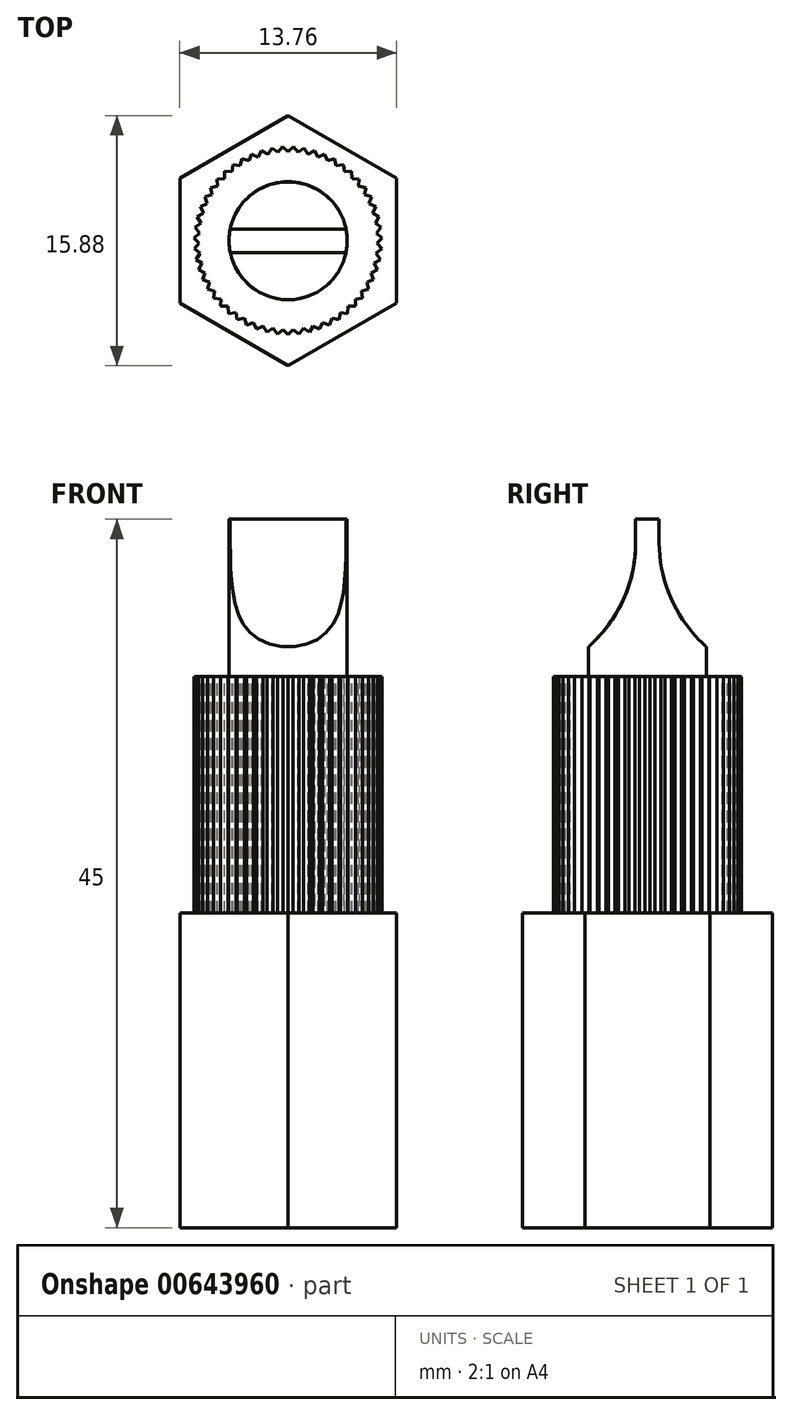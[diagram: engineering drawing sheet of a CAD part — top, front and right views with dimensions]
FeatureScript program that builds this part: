
annotation { "Feature Type Name" : "Feature", "Feature Type Description" : "" }
export const myFeature = defineFeature(function(context is Context, id is Id, definition is map)
    precondition{}
    {
        {
            var Q0;
            Q0=qCreatedBy(makeId("Top.planeOp"),FACE);
            var sketch = newSketch(context, id + "F0", { "sketchPlane" : qUnion([Q0])});
            skCircle(sketch, "E0.cCircle", {"center": v(0, 0) * mm, "radius": 7.94 * mm, "construction": true});
            skLineSegment(sketch, "E0.0", {"start": v(6.87, 3.97) * mm, "end": v(6.88, -3.97) * mm});
            skLineSegment(sketch, "E0.1", {"start": v(6.88, -3.97) * mm, "end": v(0, -7.94) * mm});
            skLineSegment(sketch, "E0.2", {"start": v(0, -7.94) * mm, "end": v(-6.88, -3.97) * mm});
            skLineSegment(sketch, "E0.3", {"start": v(-6.87, -3.97) * mm, "end": v(-6.88, 3.97) * mm});
            skLineSegment(sketch, "E0.4", {"start": v(-6.88, 3.97) * mm, "end": v(0, 7.94) * mm});
            skLineSegment(sketch, "E0.5", {"start": v(0, 7.94) * mm, "end": v(6.87, 3.97) * mm});
            skSolve(sketch);
        }
        {
            var Q0;
            Q0 = qSketchRegion(id + "F0", true);
            extrude(context, id + "F1", {"entities" : qUnion([Q0]), "depth" : 20 * mm, "offsetDistance" : 25 * mm});
        }
        {
            var Q0;
            Q0=makeQuery(id+"F1.opExtrude","CAP_FACE",FACE,{"disambiguationData":[OSD([sQuery(id+"F0.wireOp",EDGE,"E0.0"),sQuery(id+"F0.wireOp",EDGE,"E0.1"),sQuery(id+"F0.wireOp",EDGE,"E0.2"),sQuery(id+"F0.wireOp",EDGE,"E0.3"),sQuery(id+"F0.wireOp",EDGE,"E0.4"),sQuery(id+"F0.wireOp",EDGE,"E0.5")])],"isStart":false});
            var sketch = newSketch(context, id + "F2", { "sketchPlane" : qUnion([Q0])});
            skCircle(sketch, "E1", {"center": v(0, 0) * mm, "radius": 6 * mm});
            skSolve(sketch);
        }
        {
            var Q0;
            Q0=makeQuery(id+"F2.imprint","IMPRINT",FACE,{"disambiguationData":[TD([[makeQuery(id+"F2.imprint","IMPRINT",EDGE,{"derivedFrom":sQuery(id+"F2.wireOp",EDGE,"E1")}),1.0]])]});
            extrude(context, id + "F3", {"entities" : qUnion([Q0]), "operationType" : NewBodyOperationType.ADD, "depth" : 15 * mm, "offsetDistance" : 25 * mm});
        }
        {
            var Q0;
            Q0=makeQuery(id+"F3.opExtrude","CAP_FACE",FACE,{"disambiguationData":[OSD([sQuery(id+"F2.wireOp",EDGE,"E1")])],"isStart":false});
            var sketch = newSketch(context, id + "F4", { "sketchPlane" : qUnion([Q0])});
            skLineSegment(sketch, "E2", {"start": v(0, 0) * mm, "end": v(0, 6) * mm, "construction": true});
            skLineSegment(sketch, "E3", {"start": v(-0.37, 5.99) * mm, "end": v(0, 5.65) * mm});
            skLineSegment(sketch, "E4", {"start": v(0.37, 5.99) * mm, "end": v(0, 5.65) * mm});
            skSolve(sketch);
        }
        {
            var Q0;
            {var subQ0=sQuery(id+"F4.wireOp",EDGE,"E3");Q0=makeQuery(id+"F4.imprint","IMPRINT",FACE,{"disambiguationData":[TD([[makeQuery(id+"F4.imprint","IMPRINT",EDGE,{"derivedFrom":subQ0}),1.0]])]});}
            var Q1;
            Q1=makeQuery(id+"F1.opExtrude","CAP_FACE",FACE,{"disambiguationData":[OSD([sQuery(id+"F0.wireOp",EDGE,"E0.0"),sQuery(id+"F0.wireOp",EDGE,"E0.1"),sQuery(id+"F0.wireOp",EDGE,"E0.2"),sQuery(id+"F0.wireOp",EDGE,"E0.3"),sQuery(id+"F0.wireOp",EDGE,"E0.4"),sQuery(id+"F0.wireOp",EDGE,"E0.5")])],"isStart":false});
            extrude(context, id + "F5", {"entities" : qUnion([Q0]), "endBound" : BoundingType.UP_TO_SURFACE, "oppositeDirection" : true, "depth" : 25 * mm, "endBoundEntityFace" : qUnion([Q1]), "offsetDistance" : 25 * mm});
        }
        {
            var Q0;
            Q0=makeQuery(id+"F5.opExtrude","SWEPT_BODY",BODY,{"disambiguationData":[OSD([sQuery(id+"F2.wireOp",EDGE,"E1"),sQuery(id+"F4.wireOp",EDGE,"E3"),sQuery(id+"F4.wireOp",EDGE,"E4")])]});
            var Q1;
            Q1=makeQuery(id+"F3.opExtrude","CAP_EDGE",EDGE,{"disambiguationData":[OSD([sQuery(id+"F2.wireOp",EDGE,"E1")])],"isStart":false});
            circularPattern(context, id + "F6", {"entities" : qUnion([Q0]), "axis" : qUnion([Q1]), "angle" : 360 * degree, "instanceCount" : 55, "oppositeDirection" : true, "equalSpace" : true});
        }
        {
            var Q0;
            Q0=makeQuery(id+"F6.opPattern","COPY",BODY,{"derivedFrom":makeQuery(id+"F5.opExtrude","SWEPT_BODY",BODY,{"disambiguationData":[OSD([sQuery(id+"F2.wireOp",EDGE,"E1"),sQuery(id+"F4.wireOp",EDGE,"E3"),sQuery(id+"F4.wireOp",EDGE,"E4")])]}),"instanceName":"6"});
            var Q1;
            Q1=makeQuery(id+"F6.opPattern","COPY",BODY,{"derivedFrom":makeQuery(id+"F5.opExtrude","SWEPT_BODY",BODY,{"disambiguationData":[OSD([sQuery(id+"F2.wireOp",EDGE,"E1"),sQuery(id+"F4.wireOp",EDGE,"E3"),sQuery(id+"F4.wireOp",EDGE,"E4")])]}),"instanceName":"8"});
            var Q2;
            Q2=makeQuery(id+"F6.opPattern","COPY",BODY,{"derivedFrom":makeQuery(id+"F5.opExtrude","SWEPT_BODY",BODY,{"disambiguationData":[OSD([sQuery(id+"F2.wireOp",EDGE,"E1"),sQuery(id+"F4.wireOp",EDGE,"E3"),sQuery(id+"F4.wireOp",EDGE,"E4")])]}),"instanceName":"10"});
            var Q3;
            Q3=makeQuery(id+"F6.opPattern","COPY",BODY,{"derivedFrom":makeQuery(id+"F5.opExtrude","SWEPT_BODY",BODY,{"disambiguationData":[OSD([sQuery(id+"F2.wireOp",EDGE,"E1"),sQuery(id+"F4.wireOp",EDGE,"E3"),sQuery(id+"F4.wireOp",EDGE,"E4")])]}),"instanceName":"7"});
            var Q4;
            Q4=makeQuery(id+"F6.opPattern","COPY",BODY,{"derivedFrom":makeQuery(id+"F5.opExtrude","SWEPT_BODY",BODY,{"disambiguationData":[OSD([sQuery(id+"F2.wireOp",EDGE,"E1"),sQuery(id+"F4.wireOp",EDGE,"E3"),sQuery(id+"F4.wireOp",EDGE,"E4")])]}),"instanceName":"1"});
            var Q5;
            Q5=makeQuery(id+"F6.opPattern","COPY",BODY,{"derivedFrom":makeQuery(id+"F5.opExtrude","SWEPT_BODY",BODY,{"disambiguationData":[OSD([sQuery(id+"F2.wireOp",EDGE,"E1"),sQuery(id+"F4.wireOp",EDGE,"E3"),sQuery(id+"F4.wireOp",EDGE,"E4")])]}),"instanceName":"4"});
            var Q6;
            Q6=makeQuery(id+"F6.opPattern","COPY",BODY,{"derivedFrom":makeQuery(id+"F5.opExtrude","SWEPT_BODY",BODY,{"disambiguationData":[OSD([sQuery(id+"F2.wireOp",EDGE,"E1"),sQuery(id+"F4.wireOp",EDGE,"E3"),sQuery(id+"F4.wireOp",EDGE,"E4")])]}),"instanceName":"5"});
            var Q7;
            Q7=makeQuery(id+"F6.opPattern","COPY",BODY,{"derivedFrom":makeQuery(id+"F5.opExtrude","SWEPT_BODY",BODY,{"disambiguationData":[OSD([sQuery(id+"F2.wireOp",EDGE,"E1"),sQuery(id+"F4.wireOp",EDGE,"E3"),sQuery(id+"F4.wireOp",EDGE,"E4")])]}),"instanceName":"3"});
            var Q8;
            Q8=makeQuery(id+"F6.opPattern","COPY",BODY,{"derivedFrom":makeQuery(id+"F5.opExtrude","SWEPT_BODY",BODY,{"disambiguationData":[OSD([sQuery(id+"F2.wireOp",EDGE,"E1"),sQuery(id+"F4.wireOp",EDGE,"E3"),sQuery(id+"F4.wireOp",EDGE,"E4")])]}),"instanceName":"2"});
            var Q9;
            Q9=makeQuery(id+"F5.opExtrude","SWEPT_BODY",BODY,{"disambiguationData":[OSD([sQuery(id+"F2.wireOp",EDGE,"E1"),sQuery(id+"F4.wireOp",EDGE,"E3"),sQuery(id+"F4.wireOp",EDGE,"E4")])]});
            var Q10;
            Q10=makeQuery(id+"F6.opPattern","COPY",BODY,{"derivedFrom":makeQuery(id+"F5.opExtrude","SWEPT_BODY",BODY,{"disambiguationData":[OSD([sQuery(id+"F2.wireOp",EDGE,"E1"),sQuery(id+"F4.wireOp",EDGE,"E3"),sQuery(id+"F4.wireOp",EDGE,"E4")])]}),"instanceName":"9"});
            var Q11;
            Q11=makeQuery(id+"F6.opPattern","COPY",BODY,{"derivedFrom":makeQuery(id+"F5.opExtrude","SWEPT_BODY",BODY,{"disambiguationData":[OSD([sQuery(id+"F2.wireOp",EDGE,"E1"),sQuery(id+"F4.wireOp",EDGE,"E3"),sQuery(id+"F4.wireOp",EDGE,"E4")])]}),"instanceName":"11"});
            var Q12;
            Q12=makeQuery(id+"F6.opPattern","COPY",BODY,{"derivedFrom":makeQuery(id+"F5.opExtrude","SWEPT_BODY",BODY,{"disambiguationData":[OSD([sQuery(id+"F2.wireOp",EDGE,"E1"),sQuery(id+"F4.wireOp",EDGE,"E3"),sQuery(id+"F4.wireOp",EDGE,"E4")])]}),"instanceName":"12"});
            var Q13;
            Q13=makeQuery(id+"F6.opPattern","COPY",BODY,{"derivedFrom":makeQuery(id+"F5.opExtrude","SWEPT_BODY",BODY,{"disambiguationData":[OSD([sQuery(id+"F2.wireOp",EDGE,"E1"),sQuery(id+"F4.wireOp",EDGE,"E3"),sQuery(id+"F4.wireOp",EDGE,"E4")])]}),"instanceName":"13"});
            var Q14;
            Q14=makeQuery(id+"F6.opPattern","COPY",BODY,{"derivedFrom":makeQuery(id+"F5.opExtrude","SWEPT_BODY",BODY,{"disambiguationData":[OSD([sQuery(id+"F2.wireOp",EDGE,"E1"),sQuery(id+"F4.wireOp",EDGE,"E3"),sQuery(id+"F4.wireOp",EDGE,"E4")])]}),"instanceName":"14"});
            var Q15;
            Q15=makeQuery(id+"F6.opPattern","COPY",BODY,{"derivedFrom":makeQuery(id+"F5.opExtrude","SWEPT_BODY",BODY,{"disambiguationData":[OSD([sQuery(id+"F2.wireOp",EDGE,"E1"),sQuery(id+"F4.wireOp",EDGE,"E3"),sQuery(id+"F4.wireOp",EDGE,"E4")])]}),"instanceName":"15"});
            var Q16;
            Q16=makeQuery(id+"F6.opPattern","COPY",BODY,{"derivedFrom":makeQuery(id+"F5.opExtrude","SWEPT_BODY",BODY,{"disambiguationData":[OSD([sQuery(id+"F2.wireOp",EDGE,"E1"),sQuery(id+"F4.wireOp",EDGE,"E3"),sQuery(id+"F4.wireOp",EDGE,"E4")])]}),"instanceName":"16"});
            var Q17;
            Q17=makeQuery(id+"F6.opPattern","COPY",BODY,{"derivedFrom":makeQuery(id+"F5.opExtrude","SWEPT_BODY",BODY,{"disambiguationData":[OSD([sQuery(id+"F2.wireOp",EDGE,"E1"),sQuery(id+"F4.wireOp",EDGE,"E3"),sQuery(id+"F4.wireOp",EDGE,"E4")])]}),"instanceName":"17"});
            var Q18;
            Q18=makeQuery(id+"F6.opPattern","COPY",BODY,{"derivedFrom":makeQuery(id+"F5.opExtrude","SWEPT_BODY",BODY,{"disambiguationData":[OSD([sQuery(id+"F2.wireOp",EDGE,"E1"),sQuery(id+"F4.wireOp",EDGE,"E3"),sQuery(id+"F4.wireOp",EDGE,"E4")])]}),"instanceName":"18"});
            var Q19;
            Q19=makeQuery(id+"F6.opPattern","COPY",BODY,{"derivedFrom":makeQuery(id+"F5.opExtrude","SWEPT_BODY",BODY,{"disambiguationData":[OSD([sQuery(id+"F2.wireOp",EDGE,"E1"),sQuery(id+"F4.wireOp",EDGE,"E3"),sQuery(id+"F4.wireOp",EDGE,"E4")])]}),"instanceName":"19"});
            var Q20;
            Q20=makeQuery(id+"F6.opPattern","COPY",BODY,{"derivedFrom":makeQuery(id+"F5.opExtrude","SWEPT_BODY",BODY,{"disambiguationData":[OSD([sQuery(id+"F2.wireOp",EDGE,"E1"),sQuery(id+"F4.wireOp",EDGE,"E3"),sQuery(id+"F4.wireOp",EDGE,"E4")])]}),"instanceName":"20"});
            var Q21;
            Q21=makeQuery(id+"F6.opPattern","COPY",BODY,{"derivedFrom":makeQuery(id+"F5.opExtrude","SWEPT_BODY",BODY,{"disambiguationData":[OSD([sQuery(id+"F2.wireOp",EDGE,"E1"),sQuery(id+"F4.wireOp",EDGE,"E3"),sQuery(id+"F4.wireOp",EDGE,"E4")])]}),"instanceName":"21"});
            var Q22;
            Q22=makeQuery(id+"F6.opPattern","COPY",BODY,{"derivedFrom":makeQuery(id+"F5.opExtrude","SWEPT_BODY",BODY,{"disambiguationData":[OSD([sQuery(id+"F2.wireOp",EDGE,"E1"),sQuery(id+"F4.wireOp",EDGE,"E3"),sQuery(id+"F4.wireOp",EDGE,"E4")])]}),"instanceName":"22"});
            var Q23;
            Q23=makeQuery(id+"F6.opPattern","COPY",BODY,{"derivedFrom":makeQuery(id+"F5.opExtrude","SWEPT_BODY",BODY,{"disambiguationData":[OSD([sQuery(id+"F2.wireOp",EDGE,"E1"),sQuery(id+"F4.wireOp",EDGE,"E3"),sQuery(id+"F4.wireOp",EDGE,"E4")])]}),"instanceName":"23"});
            var Q24;
            Q24=makeQuery(id+"F6.opPattern","COPY",BODY,{"derivedFrom":makeQuery(id+"F5.opExtrude","SWEPT_BODY",BODY,{"disambiguationData":[OSD([sQuery(id+"F2.wireOp",EDGE,"E1"),sQuery(id+"F4.wireOp",EDGE,"E3"),sQuery(id+"F4.wireOp",EDGE,"E4")])]}),"instanceName":"24"});
            var Q25;
            Q25=makeQuery(id+"F6.opPattern","COPY",BODY,{"derivedFrom":makeQuery(id+"F5.opExtrude","SWEPT_BODY",BODY,{"disambiguationData":[OSD([sQuery(id+"F2.wireOp",EDGE,"E1"),sQuery(id+"F4.wireOp",EDGE,"E3"),sQuery(id+"F4.wireOp",EDGE,"E4")])]}),"instanceName":"25"});
            var Q26;
            Q26=makeQuery(id+"F6.opPattern","COPY",BODY,{"derivedFrom":makeQuery(id+"F5.opExtrude","SWEPT_BODY",BODY,{"disambiguationData":[OSD([sQuery(id+"F2.wireOp",EDGE,"E1"),sQuery(id+"F4.wireOp",EDGE,"E3"),sQuery(id+"F4.wireOp",EDGE,"E4")])]}),"instanceName":"26"});
            var Q27;
            Q27=makeQuery(id+"F6.opPattern","COPY",BODY,{"derivedFrom":makeQuery(id+"F5.opExtrude","SWEPT_BODY",BODY,{"disambiguationData":[OSD([sQuery(id+"F2.wireOp",EDGE,"E1"),sQuery(id+"F4.wireOp",EDGE,"E3"),sQuery(id+"F4.wireOp",EDGE,"E4")])]}),"instanceName":"27"});
            var Q28;
            Q28=makeQuery(id+"F6.opPattern","COPY",BODY,{"derivedFrom":makeQuery(id+"F5.opExtrude","SWEPT_BODY",BODY,{"disambiguationData":[OSD([sQuery(id+"F2.wireOp",EDGE,"E1"),sQuery(id+"F4.wireOp",EDGE,"E3"),sQuery(id+"F4.wireOp",EDGE,"E4")])]}),"instanceName":"28"});
            var Q29;
            Q29=makeQuery(id+"F6.opPattern","COPY",BODY,{"derivedFrom":makeQuery(id+"F5.opExtrude","SWEPT_BODY",BODY,{"disambiguationData":[OSD([sQuery(id+"F2.wireOp",EDGE,"E1"),sQuery(id+"F4.wireOp",EDGE,"E3"),sQuery(id+"F4.wireOp",EDGE,"E4")])]}),"instanceName":"29"});
            var Q30;
            Q30=makeQuery(id+"F6.opPattern","COPY",BODY,{"derivedFrom":makeQuery(id+"F5.opExtrude","SWEPT_BODY",BODY,{"disambiguationData":[OSD([sQuery(id+"F2.wireOp",EDGE,"E1"),sQuery(id+"F4.wireOp",EDGE,"E3"),sQuery(id+"F4.wireOp",EDGE,"E4")])]}),"instanceName":"30"});
            var Q31;
            Q31=makeQuery(id+"F6.opPattern","COPY",BODY,{"derivedFrom":makeQuery(id+"F5.opExtrude","SWEPT_BODY",BODY,{"disambiguationData":[OSD([sQuery(id+"F2.wireOp",EDGE,"E1"),sQuery(id+"F4.wireOp",EDGE,"E3"),sQuery(id+"F4.wireOp",EDGE,"E4")])]}),"instanceName":"31"});
            var Q32;
            Q32=makeQuery(id+"F6.opPattern","COPY",BODY,{"derivedFrom":makeQuery(id+"F5.opExtrude","SWEPT_BODY",BODY,{"disambiguationData":[OSD([sQuery(id+"F2.wireOp",EDGE,"E1"),sQuery(id+"F4.wireOp",EDGE,"E3"),sQuery(id+"F4.wireOp",EDGE,"E4")])]}),"instanceName":"32"});
            var Q33;
            Q33=makeQuery(id+"F6.opPattern","COPY",BODY,{"derivedFrom":makeQuery(id+"F5.opExtrude","SWEPT_BODY",BODY,{"disambiguationData":[OSD([sQuery(id+"F2.wireOp",EDGE,"E1"),sQuery(id+"F4.wireOp",EDGE,"E3"),sQuery(id+"F4.wireOp",EDGE,"E4")])]}),"instanceName":"33"});
            var Q34;
            Q34=makeQuery(id+"F6.opPattern","COPY",BODY,{"derivedFrom":makeQuery(id+"F5.opExtrude","SWEPT_BODY",BODY,{"disambiguationData":[OSD([sQuery(id+"F2.wireOp",EDGE,"E1"),sQuery(id+"F4.wireOp",EDGE,"E3"),sQuery(id+"F4.wireOp",EDGE,"E4")])]}),"instanceName":"34"});
            var Q35;
            Q35=makeQuery(id+"F6.opPattern","COPY",BODY,{"derivedFrom":makeQuery(id+"F5.opExtrude","SWEPT_BODY",BODY,{"disambiguationData":[OSD([sQuery(id+"F2.wireOp",EDGE,"E1"),sQuery(id+"F4.wireOp",EDGE,"E3"),sQuery(id+"F4.wireOp",EDGE,"E4")])]}),"instanceName":"35"});
            var Q36;
            Q36=makeQuery(id+"F6.opPattern","COPY",BODY,{"derivedFrom":makeQuery(id+"F5.opExtrude","SWEPT_BODY",BODY,{"disambiguationData":[OSD([sQuery(id+"F2.wireOp",EDGE,"E1"),sQuery(id+"F4.wireOp",EDGE,"E3"),sQuery(id+"F4.wireOp",EDGE,"E4")])]}),"instanceName":"36"});
            var Q37;
            Q37=makeQuery(id+"F6.opPattern","COPY",BODY,{"derivedFrom":makeQuery(id+"F5.opExtrude","SWEPT_BODY",BODY,{"disambiguationData":[OSD([sQuery(id+"F2.wireOp",EDGE,"E1"),sQuery(id+"F4.wireOp",EDGE,"E3"),sQuery(id+"F4.wireOp",EDGE,"E4")])]}),"instanceName":"37"});
            var Q38;
            Q38=makeQuery(id+"F6.opPattern","COPY",BODY,{"derivedFrom":makeQuery(id+"F5.opExtrude","SWEPT_BODY",BODY,{"disambiguationData":[OSD([sQuery(id+"F2.wireOp",EDGE,"E1"),sQuery(id+"F4.wireOp",EDGE,"E3"),sQuery(id+"F4.wireOp",EDGE,"E4")])]}),"instanceName":"38"});
            var Q39;
            Q39=makeQuery(id+"F6.opPattern","COPY",BODY,{"derivedFrom":makeQuery(id+"F5.opExtrude","SWEPT_BODY",BODY,{"disambiguationData":[OSD([sQuery(id+"F2.wireOp",EDGE,"E1"),sQuery(id+"F4.wireOp",EDGE,"E3"),sQuery(id+"F4.wireOp",EDGE,"E4")])]}),"instanceName":"39"});
            var Q40;
            Q40=makeQuery(id+"F6.opPattern","COPY",BODY,{"derivedFrom":makeQuery(id+"F5.opExtrude","SWEPT_BODY",BODY,{"disambiguationData":[OSD([sQuery(id+"F2.wireOp",EDGE,"E1"),sQuery(id+"F4.wireOp",EDGE,"E3"),sQuery(id+"F4.wireOp",EDGE,"E4")])]}),"instanceName":"40"});
            var Q41;
            Q41=makeQuery(id+"F6.opPattern","COPY",BODY,{"derivedFrom":makeQuery(id+"F5.opExtrude","SWEPT_BODY",BODY,{"disambiguationData":[OSD([sQuery(id+"F2.wireOp",EDGE,"E1"),sQuery(id+"F4.wireOp",EDGE,"E3"),sQuery(id+"F4.wireOp",EDGE,"E4")])]}),"instanceName":"41"});
            var Q42;
            Q42=makeQuery(id+"F6.opPattern","COPY",BODY,{"derivedFrom":makeQuery(id+"F5.opExtrude","SWEPT_BODY",BODY,{"disambiguationData":[OSD([sQuery(id+"F2.wireOp",EDGE,"E1"),sQuery(id+"F4.wireOp",EDGE,"E3"),sQuery(id+"F4.wireOp",EDGE,"E4")])]}),"instanceName":"42"});
            var Q43;
            Q43=makeQuery(id+"F6.opPattern","COPY",BODY,{"derivedFrom":makeQuery(id+"F5.opExtrude","SWEPT_BODY",BODY,{"disambiguationData":[OSD([sQuery(id+"F2.wireOp",EDGE,"E1"),sQuery(id+"F4.wireOp",EDGE,"E3"),sQuery(id+"F4.wireOp",EDGE,"E4")])]}),"instanceName":"43"});
            var Q44;
            Q44=makeQuery(id+"F6.opPattern","COPY",BODY,{"derivedFrom":makeQuery(id+"F5.opExtrude","SWEPT_BODY",BODY,{"disambiguationData":[OSD([sQuery(id+"F2.wireOp",EDGE,"E1"),sQuery(id+"F4.wireOp",EDGE,"E3"),sQuery(id+"F4.wireOp",EDGE,"E4")])]}),"instanceName":"44"});
            var Q45;
            Q45=makeQuery(id+"F6.opPattern","COPY",BODY,{"derivedFrom":makeQuery(id+"F5.opExtrude","SWEPT_BODY",BODY,{"disambiguationData":[OSD([sQuery(id+"F2.wireOp",EDGE,"E1"),sQuery(id+"F4.wireOp",EDGE,"E3"),sQuery(id+"F4.wireOp",EDGE,"E4")])]}),"instanceName":"45"});
            var Q46;
            Q46=makeQuery(id+"F6.opPattern","COPY",BODY,{"derivedFrom":makeQuery(id+"F5.opExtrude","SWEPT_BODY",BODY,{"disambiguationData":[OSD([sQuery(id+"F2.wireOp",EDGE,"E1"),sQuery(id+"F4.wireOp",EDGE,"E3"),sQuery(id+"F4.wireOp",EDGE,"E4")])]}),"instanceName":"46"});
            var Q47;
            Q47=makeQuery(id+"F6.opPattern","COPY",BODY,{"derivedFrom":makeQuery(id+"F5.opExtrude","SWEPT_BODY",BODY,{"disambiguationData":[OSD([sQuery(id+"F2.wireOp",EDGE,"E1"),sQuery(id+"F4.wireOp",EDGE,"E3"),sQuery(id+"F4.wireOp",EDGE,"E4")])]}),"instanceName":"47"});
            var Q48;
            Q48=makeQuery(id+"F6.opPattern","COPY",BODY,{"derivedFrom":makeQuery(id+"F5.opExtrude","SWEPT_BODY",BODY,{"disambiguationData":[OSD([sQuery(id+"F2.wireOp",EDGE,"E1"),sQuery(id+"F4.wireOp",EDGE,"E3"),sQuery(id+"F4.wireOp",EDGE,"E4")])]}),"instanceName":"48"});
            var Q49;
            Q49=makeQuery(id+"F6.opPattern","COPY",BODY,{"derivedFrom":makeQuery(id+"F5.opExtrude","SWEPT_BODY",BODY,{"disambiguationData":[OSD([sQuery(id+"F2.wireOp",EDGE,"E1"),sQuery(id+"F4.wireOp",EDGE,"E3"),sQuery(id+"F4.wireOp",EDGE,"E4")])]}),"instanceName":"49"});
            var Q50;
            Q50=makeQuery(id+"F6.opPattern","COPY",BODY,{"derivedFrom":makeQuery(id+"F5.opExtrude","SWEPT_BODY",BODY,{"disambiguationData":[OSD([sQuery(id+"F2.wireOp",EDGE,"E1"),sQuery(id+"F4.wireOp",EDGE,"E3"),sQuery(id+"F4.wireOp",EDGE,"E4")])]}),"instanceName":"50"});
            var Q51;
            Q51=makeQuery(id+"F6.opPattern","COPY",BODY,{"derivedFrom":makeQuery(id+"F5.opExtrude","SWEPT_BODY",BODY,{"disambiguationData":[OSD([sQuery(id+"F2.wireOp",EDGE,"E1"),sQuery(id+"F4.wireOp",EDGE,"E3"),sQuery(id+"F4.wireOp",EDGE,"E4")])]}),"instanceName":"51"});
            var Q52;
            Q52=makeQuery(id+"F6.opPattern","COPY",BODY,{"derivedFrom":makeQuery(id+"F5.opExtrude","SWEPT_BODY",BODY,{"disambiguationData":[OSD([sQuery(id+"F2.wireOp",EDGE,"E1"),sQuery(id+"F4.wireOp",EDGE,"E3"),sQuery(id+"F4.wireOp",EDGE,"E4")])]}),"instanceName":"52"});
            var Q53;
            Q53=makeQuery(id+"F6.opPattern","COPY",BODY,{"derivedFrom":makeQuery(id+"F5.opExtrude","SWEPT_BODY",BODY,{"disambiguationData":[OSD([sQuery(id+"F2.wireOp",EDGE,"E1"),sQuery(id+"F4.wireOp",EDGE,"E3"),sQuery(id+"F4.wireOp",EDGE,"E4")])]}),"instanceName":"53"});
            var Q54;
            Q54=makeQuery(id+"F6.opPattern","COPY",BODY,{"derivedFrom":makeQuery(id+"F5.opExtrude","SWEPT_BODY",BODY,{"disambiguationData":[OSD([sQuery(id+"F2.wireOp",EDGE,"E1"),sQuery(id+"F4.wireOp",EDGE,"E3"),sQuery(id+"F4.wireOp",EDGE,"E4")])]}),"instanceName":"54"});
            var Q55;
            Q55=makeQuery(id+"F1.opExtrude","SWEPT_BODY",BODY,{"disambiguationData":[OSD([sQuery(id+"F0.wireOp",EDGE,"E0.0"),sQuery(id+"F0.wireOp",EDGE,"E0.1"),sQuery(id+"F0.wireOp",EDGE,"E0.2"),sQuery(id+"F0.wireOp",EDGE,"E0.3"),sQuery(id+"F0.wireOp",EDGE,"E0.4"),sQuery(id+"F0.wireOp",EDGE,"E0.5")])]});
            booleanBodies(context, id + "F7", {"operationType" : BooleanOperationType.SUBTRACTION, "tools" : qUnion([Q0, Q1, Q2, Q3, Q4, Q5, Q6, Q7, Q8, Q9, Q10, Q11, Q12, Q13, Q14, Q15, Q16, Q17, Q18, Q19, Q20, Q21, Q22, Q23, Q24, Q25, Q26, Q27, Q28, Q29, Q30, Q31, Q32, Q33, Q34, Q35, Q36, Q37, Q38, Q39, Q40, Q41, Q42, Q43, Q44, Q45, Q46, Q47, Q48, Q49, Q50, Q51, Q52, Q53, Q54]), "targets" : qUnion([Q55])});
        }
        {
            var Q0;
            Q0=makeQuery(id+"F3.opExtrude","CAP_FACE",FACE,{"disambiguationData":[OSD([sQuery(id+"F2.wireOp",EDGE,"E1")])],"isStart":false});
            var sketch = newSketch(context, id + "F8", { "sketchPlane" : qUnion([Q0])});
            skCircle(sketch, "E5", {"center": v(0, 0) * mm, "radius": 3.75 * mm});
            skSolve(sketch);
        }
        {
            var Q0;
            Q0=makeQuery(id+"F8.imprint","IMPRINT",FACE,{"disambiguationData":[TD([[makeQuery(id+"F8.imprint","IMPRINT",EDGE,{"derivedFrom":sQuery(id+"F8.wireOp",EDGE,"E5")}),1.0]])]});
            extrude(context, id + "F9", {"entities" : qUnion([Q0]), "operationType" : NewBodyOperationType.ADD, "depth" : 10 * mm, "offsetDistance" : 25 * mm});
        }
        {
            var Q0;
            Q0=makeQuery(id+"F1.opExtrude","SWEPT_FACE",FACE,{"disambiguationData":[OSD([sQuery(id+"F0.wireOp",EDGE,"E0.3")])]});
            var sketch = newSketch(context, id + "F10", { "sketchPlane" : qUnion([Q0])});
            skLineSegment(sketch, "E6", {"start": v(-0.75, 50) * mm, "end": v(-0.75, 43.5) * mm});
            skLineSegment(sketch, "E7", {"start": v(-4.25, 36.5) * mm, "end": v(-4.25, 50) * mm});
            skArc(sketch, "E8", {"start": v(-0.75, 43.5) * mm, "mid": v(-1.67, 39.59) * mm, "end": v(-4.25, 36.5) * mm});
            skLineSegment(sketch, "E9", {"start": v(-0.75, 49.5) * mm, "end": v(-0.75, 50) * mm});
            skLineSegment(sketch, "E10", {"start": v(0, 0) * mm, "end": v(0, 50) * mm, "construction": true});
            skLineSegment(sketch, "E11", {"start": v(-0.75, 50) * mm, "end": v(0, 50) * mm, "construction": true});
            skLineSegment(sketch, "E12", {"start": v(-0.75, 50) * mm, "end": v(-4.25, 50) * mm});
            skArc(sketch, "E13.MirrorCS", {"start": v(0.75, 43.5) * mm, "mid": v(1.67, 39.59) * mm, "end": v(4.25, 36.5) * mm});
            skLineSegment(sketch, "E14.MirrorCS", {"start": v(4.25, 36.5) * mm, "end": v(4.25, 50) * mm});
            skLineSegment(sketch, "E15.MirrorCS", {"start": v(0.75, 50) * mm, "end": v(4.25, 50) * mm});
            skLineSegment(sketch, "E16.MirrorCS", {"start": v(0.75, 50) * mm, "end": v(0.75, 43.5) * mm});
            skSolve(sketch);
        }
        {
            var Q0;
            Q0=makeQuery(id+"F10.imprint","IMPRINT",FACE,{"disambiguationData":[TD([[makeQuery(id+"F10.imprint","IMPRINT",EDGE,{"derivedFrom":sQuery(id+"F10.wireOp",EDGE,"E6")}),-1.0]])]});
            var Q1;
            Q1=makeQuery(id+"F10.imprint","IMPRINT",FACE,{"disambiguationData":[TD([[makeQuery(id+"F10.imprint","IMPRINT",EDGE,{"derivedFrom":sQuery(id+"F10.wireOp",EDGE,"E13.MirrorCS")}),1.0]])]});
            extrude(context, id + "F11", {"entities" : qUnion([Q0, Q1]), "operationType" : NewBodyOperationType.REMOVE, "oppositeDirection" : true, "depth" : 25 * mm, "offsetDistance" : 25 * mm});
        }
    });
